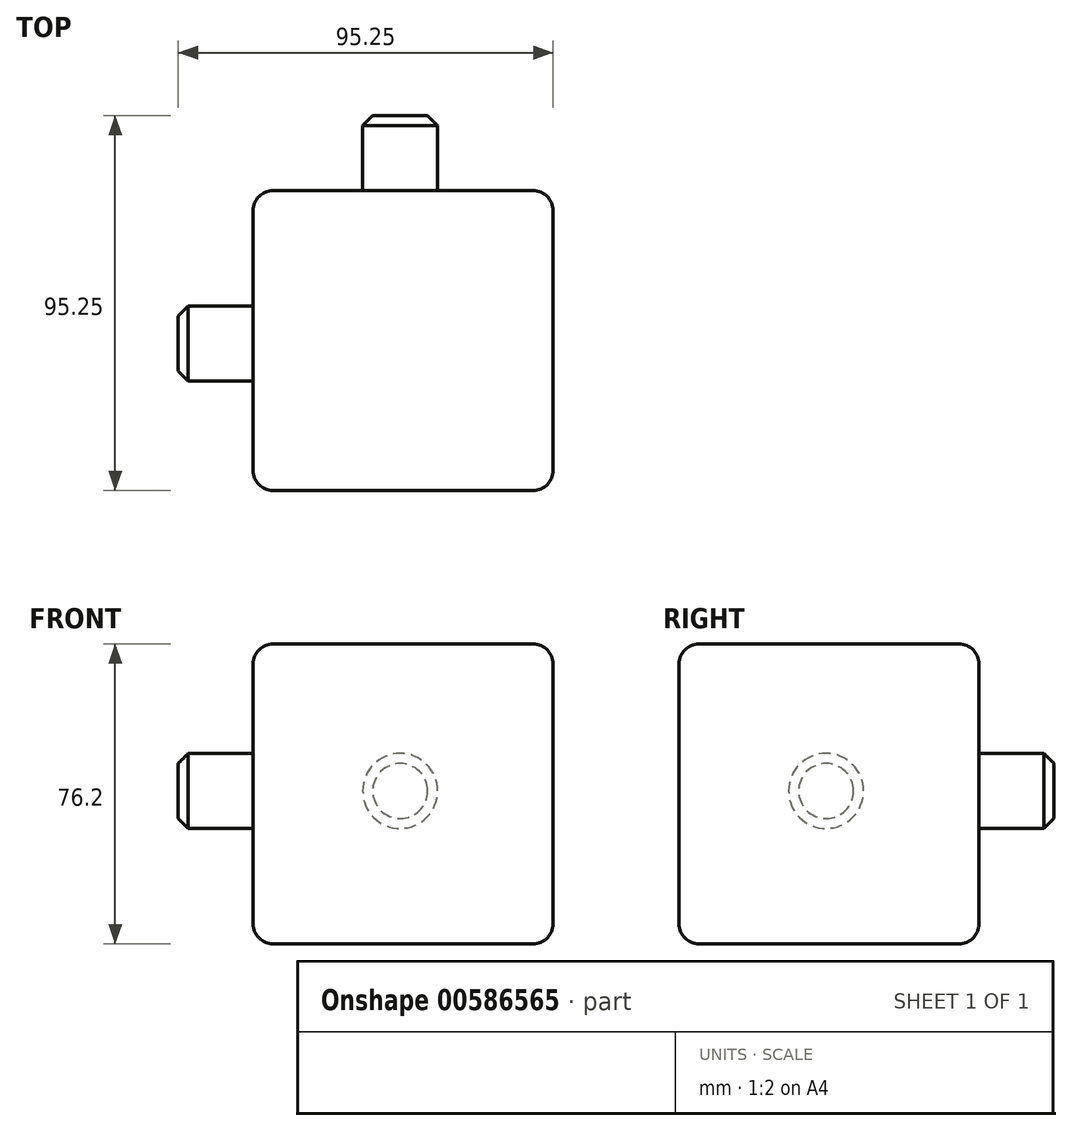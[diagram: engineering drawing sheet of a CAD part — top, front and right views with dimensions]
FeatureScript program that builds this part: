
annotation { "Feature Type Name" : "Feature", "Feature Type Description" : "" }
export const myFeature = defineFeature(function(context is Context, id is Id, definition is map)
    precondition{}
    {
        {
            var Q0;
            Q0=qCreatedBy(makeId("Top.planeOp"),FACE);
            var sketch = newSketch(context, id + "F0", { "sketchPlane" : qUnion([Q0])});
            skLineSegment(sketch, "E0.bottom", {"start": v(-37.34, -39.75) * mm, "end": v(38.86, -39.75) * mm});
            skLineSegment(sketch, "E0.top", {"start": v(-37.34, 36.45) * mm, "end": v(38.86, 36.45) * mm});
            skLineSegment(sketch, "E0.left", {"start": v(-37.34, -39.75) * mm, "end": v(-37.34, 36.45) * mm});
            skLineSegment(sketch, "E0.right", {"start": v(38.86, -39.75) * mm, "end": v(38.86, 36.45) * mm});
            skSolve(sketch);
        }
        {
            var Q0;
            Q0=makeQuery(id+"F0.imprint","IMPRINT",FACE,{"disambiguationData":[TD([[makeQuery(id+"F0.imprint","IMPRINT",EDGE,{"derivedFrom":sQuery(id+"F0.wireOp",EDGE,"E0.bottom")}),1.0]])]});
            extrude(context, id + "F1", {"entities" : qUnion([Q0]), "depth" : 76.2 * mm, "offsetDistance" : 25.4 * mm});
        }
        {
            var Q0;
            Q0=makeQuery(id+"F1.opExtrude","SWEPT_FACE",FACE,{"disambiguationData":[OSD([sQuery(id+"F0.wireOp",EDGE,"E0.bottom")])]});
            var Q1;
            Q1=makeQuery(id+"F1.opExtrude","CAP_FACE",FACE,{"disambiguationData":[OSD([sQuery(id+"F0.wireOp",EDGE,"E0.bottom"),sQuery(id+"F0.wireOp",EDGE,"E0.top"),sQuery(id+"F0.wireOp",EDGE,"E0.left"),sQuery(id+"F0.wireOp",EDGE,"E0.right")])],"isStart":false});
            var Q2;
            Q2=makeQuery(id+"F1.opExtrude","SWEPT_FACE",FACE,{"disambiguationData":[OSD([sQuery(id+"F0.wireOp",EDGE,"E0.right")])]});
            var Q3;
            Q3=makeQuery(id+"F1.opExtrude","SWEPT_FACE",FACE,{"disambiguationData":[OSD([sQuery(id+"F0.wireOp",EDGE,"E0.top")])]});
            var Q4;
            Q4=makeQuery(id+"F1.opExtrude","CAP_FACE",FACE,{"disambiguationData":[OSD([sQuery(id+"F0.wireOp",EDGE,"E0.bottom"),sQuery(id+"F0.wireOp",EDGE,"E0.top"),sQuery(id+"F0.wireOp",EDGE,"E0.left"),sQuery(id+"F0.wireOp",EDGE,"E0.right")])],"isStart":true});
            fillet(context, id + "F2", {"entities" : qUnion([Q0, Q1, Q2, Q3, Q4]), "radius" : 5.08 * mm, "tangentPropagation" : true, "allowEdgeOverflow" : false});
        }
        {
            var Q0;
            Q0=makeQuery(id+"F1.opExtrude","SWEPT_FACE",FACE,{"disambiguationData":[OSD([sQuery(id+"F0.wireOp",EDGE,"E0.top")])]});
            var sketch = newSketch(context, id + "F3", { "sketchPlane" : qUnion([Q0])});
            skLineSegment(sketch, "E1", {"start": v(-33.78, 5.08) * mm, "end": v(32.26, 71.12) * mm, "construction": true});
            skCircle(sketch, "E2", {"center": v(0, 38.86) * mm, "radius": 9.53 * mm});
            skSolve(sketch);
        }
        {
            var Q0;
            Q0 = qSketchRegion(id + "F3", true);
            extrude(context, id + "F4", {"entities" : qUnion([Q0]), "operationType" : NewBodyOperationType.ADD, "depth" : 19.05 * mm, "offsetDistance" : 25.4 * mm});
        }
        {
            var Q0;
            Q0=makeQuery(id+"F4.opExtrude","CAP_EDGE",EDGE,{"disambiguationData":[OSD([sQuery(id+"F3.wireOp",EDGE,"E2")])],"isStart":false});
            chamfer(context, id + "F5", {"entities" : qUnion([Q0]), "width" : 2.54 * mm, "tangentPropagation" : true});
        }
        {
            var Q0;
            Q0=makeQuery(id+"F1.opExtrude","SWEPT_FACE",FACE,{"disambiguationData":[OSD([sQuery(id+"F0.wireOp",EDGE,"E0.left")])]});
            var sketch = newSketch(context, id + "F6", { "sketchPlane" : qUnion([Q0])});
            skLineSegment(sketch, "E3", {"start": v(-199.28, 55.12) * mm, "end": v(-133.24, 121.16) * mm, "construction": true});
            skCircle(sketch, "E4", {"center": v(-165.5, 88.9) * mm, "radius": 9.53 * mm});
            skLineSegment(sketch, "E5", {"start": v(-31.37, 5.08) * mm, "end": v(34.67, 71.12) * mm, "construction": true});
            skCircle(sketch, "E6", {"center": v(2.4, 38.86) * mm, "radius": 9.53 * mm});
            skSolve(sketch);
        }
        {
            var Q0;
            Q0=makeQuery(id+"F6.imprint","IMPRINT",FACE,{"disambiguationData":[TD([[makeQuery(id+"F6.imprint","IMPRINT",EDGE,{"derivedFrom":sQuery(id+"F6.wireOp",EDGE,"E6")}),1.0]])]});
            extrude(context, id + "F7", {"entities" : qUnion([Q0]), "operationType" : NewBodyOperationType.ADD, "depth" : 19.05 * mm, "offsetDistance" : 25.4 * mm});
        }
        {
            var Q0;
            Q0=makeQuery(id+"F7.opExtrude","CAP_EDGE",EDGE,{"disambiguationData":[OSD([sQuery(id+"F6.wireOp",EDGE,"E6")])],"isStart":false});
            chamfer(context, id + "F8", {"entities" : qUnion([Q0]), "width" : 2.54 * mm, "tangentPropagation" : true});
        }
    });
